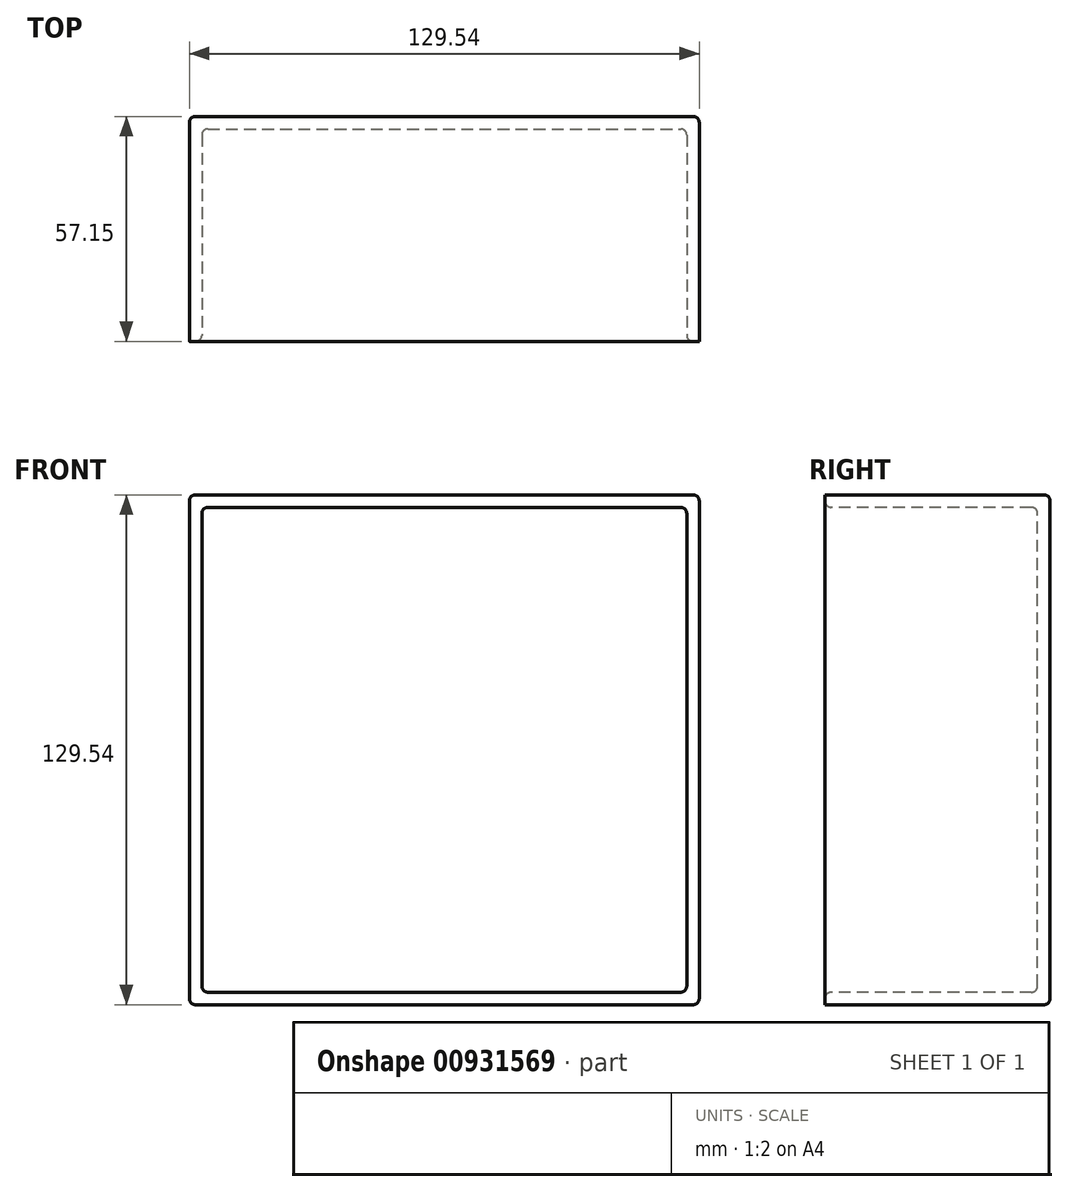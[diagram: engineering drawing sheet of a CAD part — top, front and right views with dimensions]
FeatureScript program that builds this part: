
annotation { "Feature Type Name" : "Feature", "Feature Type Description" : "" }
export const myFeature = defineFeature(function(context is Context, id is Id, definition is map)
    precondition{}
    {
        {
            var Q0;
            Q0=qCreatedBy(makeId("Front.planeOp"),FACE);
            var sketch = newSketch(context, id + "F0", { "sketchPlane" : qUnion([Q0])});
            skLineSegment(sketch, "E0.bottom", {"start": v(0, 0) * mm, "end": v(129.54, 0) * mm});
            skLineSegment(sketch, "E0.top", {"start": v(0, 129.54) * mm, "end": v(129.54, 129.54) * mm});
            skLineSegment(sketch, "E0.left", {"start": v(0, 0) * mm, "end": v(0, 129.54) * mm});
            skLineSegment(sketch, "E0.right", {"start": v(129.54, 0) * mm, "end": v(129.54, 129.54) * mm});
            skSolve(sketch);
        }
        {
            var Q0;
            Q0=makeQuery(id+"F0.imprint","IMPRINT",FACE,{"disambiguationData":[TD([[makeQuery(id+"F0.imprint","IMPRINT",EDGE,{"derivedFrom":sQuery(id+"F0.wireOp",EDGE,"E0.bottom")}),1.0]])]});
            extrude(context, id + "F1", {"entities" : qUnion([Q0]), "oppositeDirection" : true, "depth" : 57.15 * mm, "offsetDistance" : 25.4 * mm});
        }
        {
            var Q0;
            Q0=makeQuery(id+"F1.opExtrude","CAP_FACE",FACE,{"disambiguationData":[OSD([sQuery(id+"F0.wireOp",EDGE,"E0.bottom"),sQuery(id+"F0.wireOp",EDGE,"E0.top"),sQuery(id+"F0.wireOp",EDGE,"E0.left"),sQuery(id+"F0.wireOp",EDGE,"E0.right")])],"isStart":true});
            shell(context, id + "F2", {"entities" : qUnion([Q0]), "thickness" : 3.17 * mm});
        }
        {
            var Q0;
            Q0=makeQuery(id+"F2.opShell","OFFSET_EDGE",EDGE,{"disambiguationData":[OSD([sQuery(id+"F0.wireOp",EDGE,"E0.top"),sQuery(id+"F0.wireOp",EDGE,"E0.left")])]});
            var Q1;
            {var subQ0=sQuery(id+"F0.wireOp",EDGE,"E0.top");Q1=makeQuery(id+"F2.opShell","OFFSET_EDGE",EDGE,{"disambiguationData":[OSD([subQ0]),TDD([makeQuery(id+"F1.opExtrude","CAP_EDGE",EDGE,{"disambiguationData":[OSD([subQ0])],"isStart":false})])]});}
            var Q2;
            {var subQ0=sQuery(id+"F0.wireOp",EDGE,"E0.left");Q2=makeQuery(id+"F2.opShell","OFFSET_EDGE",EDGE,{"disambiguationData":[OSD([subQ0]),TDD([makeQuery(id+"F1.opExtrude","CAP_EDGE",EDGE,{"disambiguationData":[OSD([subQ0])],"isStart":false})])]});}
            var Q3;
            Q3=makeQuery(id+"F2.opShell","OFFSET_EDGE",EDGE,{"disambiguationData":[OSD([sQuery(id+"F0.wireOp",EDGE,"E0.bottom"),sQuery(id+"F0.wireOp",EDGE,"E0.left")])]});
            var Q4;
            {var subQ0=sQuery(id+"F0.wireOp",EDGE,"E0.bottom");Q4=makeQuery(id+"F2.opShell","OFFSET_EDGE",EDGE,{"disambiguationData":[OSD([subQ0]),TDD([makeQuery(id+"F1.opExtrude","CAP_EDGE",EDGE,{"disambiguationData":[OSD([subQ0])],"isStart":false})])]});}
            var Q5;
            {var subQ0=sQuery(id+"F0.wireOp",EDGE,"E0.right");Q5=makeQuery(id+"F2.opShell","OFFSET_EDGE",EDGE,{"disambiguationData":[OSD([subQ0]),TDD([makeQuery(id+"F1.opExtrude","CAP_EDGE",EDGE,{"disambiguationData":[OSD([subQ0])],"isStart":false})])]});}
            var Q6;
            Q6=makeQuery(id+"F2.opShell","OFFSET_EDGE",EDGE,{"disambiguationData":[OSD([sQuery(id+"F0.wireOp",EDGE,"E0.top"),sQuery(id+"F0.wireOp",EDGE,"E0.right")])]});
            var Q7;
            Q7=makeQuery(id+"F2.opShell","OFFSET_EDGE",EDGE,{"disambiguationData":[OSD([sQuery(id+"F0.wireOp",EDGE,"E0.bottom"),sQuery(id+"F0.wireOp",EDGE,"E0.right")])]});
            fillet(context, id + "F3", {"entities" : qUnion([Q0, Q1, Q2, Q3, Q4, Q5, Q6, Q7]), "radius" : 1.52 * mm, "tangentPropagation" : true, "allowEdgeOverflow" : false});
        }
        {
            var Q0;
            Q0=makeQuery(id+"F1.opExtrude","SWEPT_EDGE",EDGE,{"disambiguationData":[OSD([sQuery(id+"F0.wireOp",EDGE,"E0.bottom"),sQuery(id+"F0.wireOp",EDGE,"E0.right")])]});
            var Q1;
            Q1=makeQuery(id+"F1.opExtrude","CAP_EDGE",EDGE,{"disambiguationData":[OSD([sQuery(id+"F0.wireOp",EDGE,"E0.bottom")])],"isStart":false});
            var Q2;
            Q2=makeQuery(id+"F1.opExtrude","CAP_EDGE",EDGE,{"disambiguationData":[OSD([sQuery(id+"F0.wireOp",EDGE,"E0.right")])],"isStart":false});
            var Q3;
            Q3=makeQuery(id+"F1.opExtrude","SWEPT_EDGE",EDGE,{"disambiguationData":[OSD([sQuery(id+"F0.wireOp",EDGE,"E0.top"),sQuery(id+"F0.wireOp",EDGE,"E0.right")])]});
            var Q4;
            Q4=makeQuery(id+"F1.opExtrude","CAP_EDGE",EDGE,{"disambiguationData":[OSD([sQuery(id+"F0.wireOp",EDGE,"E0.top")])],"isStart":false});
            var Q5;
            Q5=makeQuery(id+"F1.opExtrude","SWEPT_EDGE",EDGE,{"disambiguationData":[OSD([sQuery(id+"F0.wireOp",EDGE,"E0.top"),sQuery(id+"F0.wireOp",EDGE,"E0.left")])]});
            var Q6;
            Q6=makeQuery(id+"F1.opExtrude","CAP_EDGE",EDGE,{"disambiguationData":[OSD([sQuery(id+"F0.wireOp",EDGE,"E0.left")])],"isStart":false});
            var Q7;
            Q7=makeQuery(id+"F1.opExtrude","SWEPT_EDGE",EDGE,{"disambiguationData":[OSD([sQuery(id+"F0.wireOp",EDGE,"E0.bottom"),sQuery(id+"F0.wireOp",EDGE,"E0.left")])]});
            fillet(context, id + "F4", {"entities" : qUnion([Q0, Q1, Q2, Q3, Q4, Q5, Q6, Q7]), "radius" : 1.52 * mm, "tangentPropagation" : true, "allowEdgeOverflow" : false});
        }
        {
            var Q0;
            {var subQ0=sQuery(id+"F0.wireOp",EDGE,"E0.bottom");Q0=makeQuery(id+"F2.opShell","OFFSET_EDGE",EDGE,{"disambiguationData":[OSD([subQ0]),TDD([makeQuery(id+"F1.opExtrude","CAP_EDGE",EDGE,{"disambiguationData":[OSD([subQ0])],"isStart":true})])]});}
            fillet(context, id + "F5", {"entities" : qUnion([Q0]), "radius" : 1.52 * mm, "tangentPropagation" : true, "allowEdgeOverflow" : false});
        }
    });
